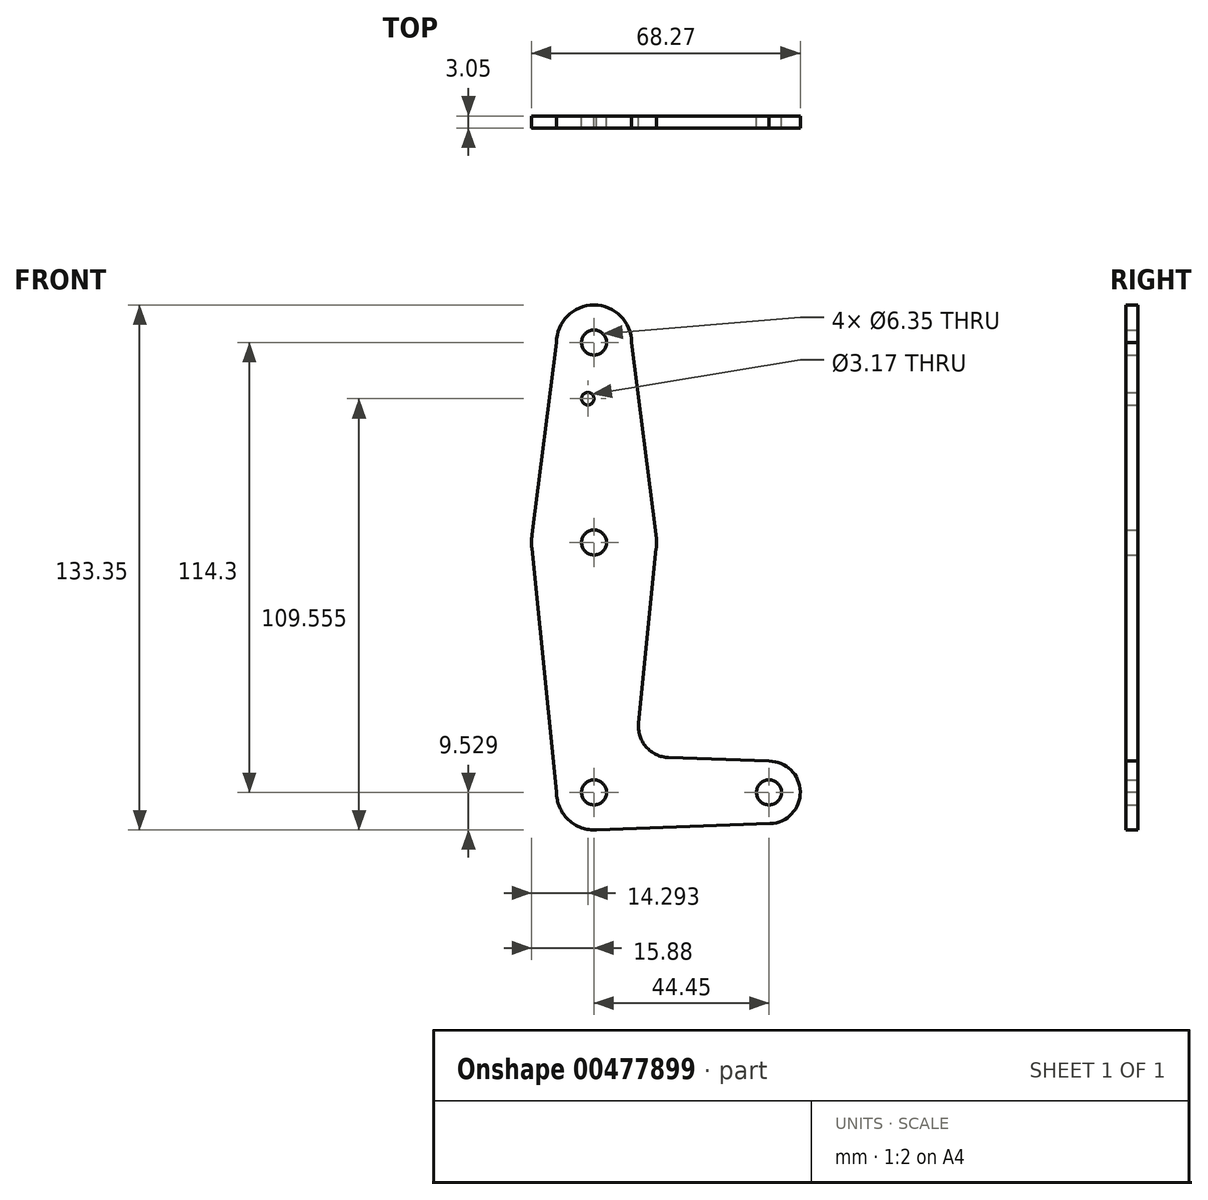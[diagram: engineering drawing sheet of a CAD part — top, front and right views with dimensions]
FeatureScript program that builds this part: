
annotation { "Feature Type Name" : "Feature", "Feature Type Description" : "" }
export const myFeature = defineFeature(function(context is Context, id is Id, definition is map)
    precondition{}
    {
        {
            var Q0;
            Q0=qCreatedBy(makeId("Front.planeOp"),FACE);
            var sketch = newSketch(context, id + "F0", { "sketchPlane" : qUnion([Q0])});
            skLineSegment(sketch, "E0", {"start": v(0, 76.59) * mm, "end": v(0, 25.79) * mm, "construction": true});
            skLineSegment(sketch, "E1", {"start": v(0, 25.79) * mm, "end": v(0, -37.71) * mm, "construction": true});
            skLineSegment(sketch, "E2", {"start": v(0, -37.71) * mm, "end": v(44.45, -37.71) * mm, "construction": true});
            skCircle(sketch, "E3", {"center": v(0, 76.59) * mm, "radius": 9.53 * mm});
            skCircle(sketch, "E4", {"center": v(0, -37.71) * mm, "radius": 9.53 * mm});
            skCircle(sketch, "E5", {"center": v(44.45, -37.71) * mm, "radius": 7.94 * mm});
            skCircle(sketch, "E6", {"center": v(0, 25.79) * mm, "radius": 15.88 * mm});
            skLineSegment(sketch, "E7", {"start": v(-9.53, 76.59) * mm, "end": v(-15.75, 27.8) * mm});
            skLineSegment(sketch, "E8", {"start": v(9.53, 76.59) * mm, "end": v(15.75, 27.8) * mm});
            skLineSegment(sketch, "E9", {"start": v(0, -47.24) * mm, "end": v(44.73, -45.64) * mm});
            skLineSegment(sketch, "E10", {"start": v(0, 25.79) * mm, "end": v(0, 62.31) * mm});
            skCircle(sketch, "E11", {"center": v(0, 76.59) * mm, "radius": 3.18 * mm});
            skCircle(sketch, "E12", {"center": v(0, 25.79) * mm, "radius": 3.18 * mm});
            skCircle(sketch, "E13", {"center": v(0, -37.71) * mm, "radius": 3.18 * mm});
            skCircle(sketch, "E14", {"center": v(44.45, -37.71) * mm, "radius": 3.18 * mm});
            skCircle(sketch, "E15", {"center": v(-1.59, 62.31) * mm, "radius": 1.59 * mm});
            skLineSegment(sketch, "E16", {"start": v(-9.52, -37.64) * mm, "end": v(-15.8, 24.19) * mm});
            skLineSegment(sketch, "E17", {"start": v(11.3, -20.12) * mm, "end": v(15.8, 24.19) * mm});
            skLineSegment(sketch, "E18", {"start": v(18.93, -28.86) * mm, "end": v(44.45, -29.77) * mm});
            skArc(sketch, "E19.filletArc", {"start": v(11.3, -20.12) * mm, "mid": v(13.22, -26.14) * mm, "end": v(18.93, -28.86) * mm});
            skSolve(sketch);
        }
        {
            var Q0;
            Q0 = qSketchRegion(id + "F0", true);
            extrude(context, id + "F1", {"entities" : qUnion([Q0]), "depth" : 3.05 * mm});
        }
    });
